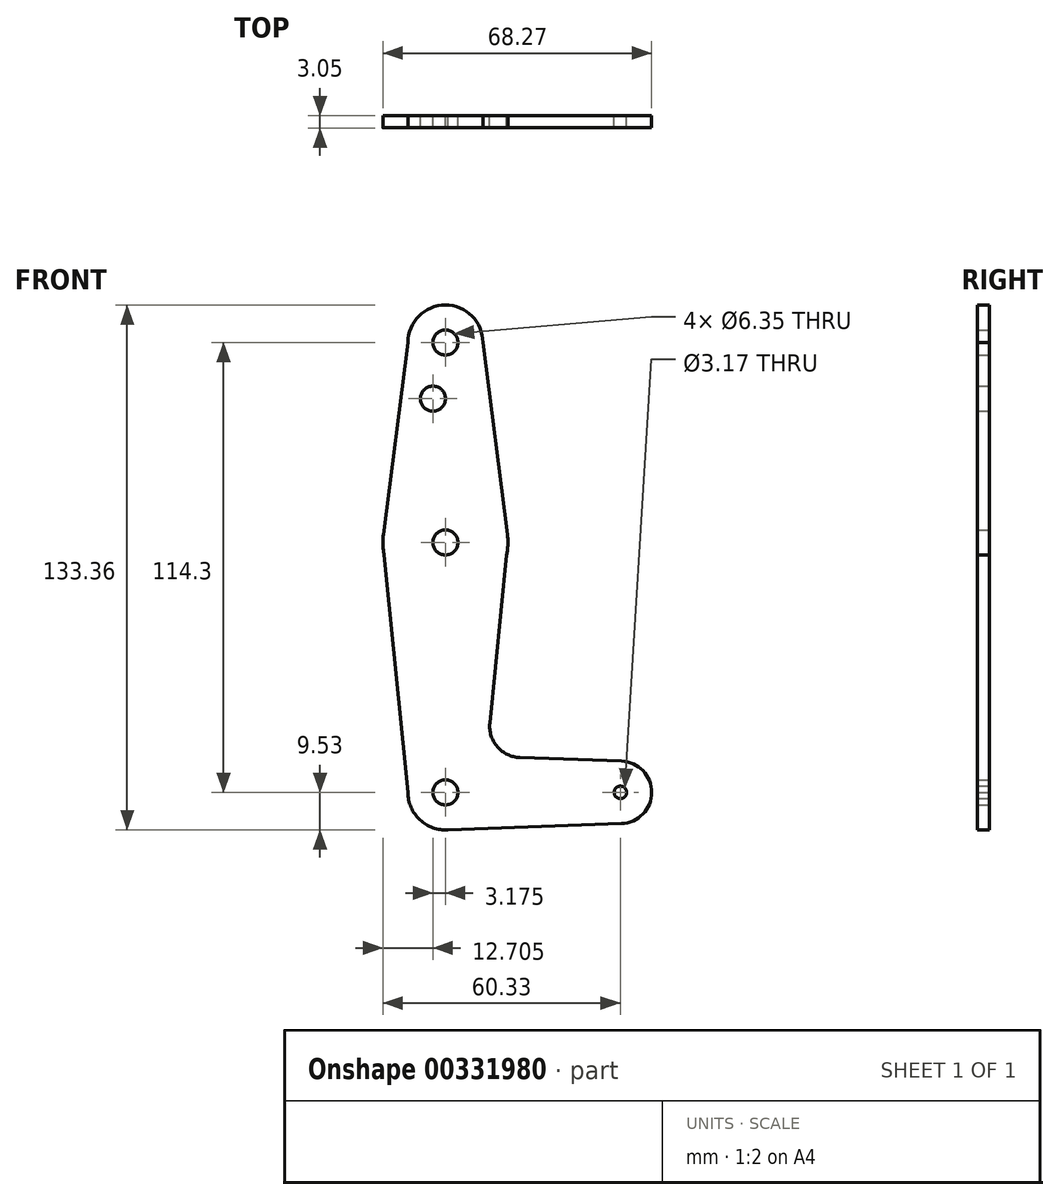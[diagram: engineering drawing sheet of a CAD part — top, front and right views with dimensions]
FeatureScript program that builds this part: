
annotation { "Feature Type Name" : "Feature", "Feature Type Description" : "" }
export const myFeature = defineFeature(function(context is Context, id is Id, definition is map)
    precondition{}
    {
        {
            var Q0;
            Q0=qCreatedBy(makeId("Front.planeOp"),FACE);
            var sketch = newSketch(context, id + "F0", { "sketchPlane" : qUnion([Q0])});
            skLineSegment(sketch, "E0", {"start": v(0, 0) * mm, "end": v(0, 114.3) * mm, "construction": true});
            skLineSegment(sketch, "E1", {"start": v(0, 0) * mm, "end": v(44.45, 0) * mm, "construction": true});
            skCircle(sketch, "E2", {"center": v(0, 114.3) * mm, "radius": 9.53 * mm});
            skCircle(sketch, "E3", {"center": v(0, 0) * mm, "radius": 9.53 * mm});
            skCircle(sketch, "E4", {"center": v(44.45, 0) * mm, "radius": 7.94 * mm});
            skCircle(sketch, "E5", {"center": v(0, 63.5) * mm, "radius": 15.88 * mm});
            skLineSegment(sketch, "E6", {"start": v(0, -9.53) * mm, "end": v(44.73, -7.93) * mm});
            skLineSegment(sketch, "E7", {"start": v(18.91, 8.85) * mm, "end": v(44.73, 7.93) * mm});
            skLineSegment(sketch, "E8", {"start": v(9.53, 114.3) * mm, "end": v(15.75, 65.5) * mm});
            skLineSegment(sketch, "E9", {"start": v(-9.53, 114.3) * mm, "end": v(-15.75, 65.5) * mm});
            skLineSegment(sketch, "E10", {"start": v(-15.88, 63.5) * mm, "end": v(-9.52, 0) * mm});
            skLineSegment(sketch, "E11", {"start": v(15.88, 63.5) * mm, "end": v(11.28, 17.59) * mm});
            skCircle(sketch, "E12", {"center": v(0, 114.3) * mm, "radius": 3.18 * mm});
            skCircle(sketch, "E13", {"center": v(0, 63.5) * mm, "radius": 3.18 * mm});
            skCircle(sketch, "E14", {"center": v(0, 0) * mm, "radius": 3.18 * mm});
            skCircle(sketch, "E15", {"center": v(44.45, 0) * mm, "radius": 1.59 * mm});
            skCircle(sketch, "E16", {"center": v(-3.18, 100.03) * mm, "radius": 3.18 * mm});
            skArc(sketch, "E17.filletArc", {"start": v(11.28, 17.59) * mm, "mid": v(13.2, 11.57) * mm, "end": v(18.91, 8.85) * mm});
            skSolve(sketch);
        }
        {
            var Q0;
            Q0 = qSketchRegion(id + "F0", true);
            extrude(context, id + "F1", {"entities" : qUnion([Q0]), "depth" : 3.05 * mm});
        }
    });
